# Revit family: Pojemnik_na_papier_toaletowy_ZEN S
name_source: partatom
category: Furniture
units: mm (PartAtom-declared; Revit-internal decimal feet)

## family parameters
Always vertical = Yes
Cut with Voids When Loaded = No
Host = Wall
Room Calculation Point = No
Shared = No

## types (1)
- Type 1
    Color / Kolor = White / Biały
    Depth / Glebokosc = 130 mm  [stored 0.426509 ft]
    Description = Pojemnik na papier toaletowy ZEN S wykonany jest z odpornego na uszkodzenia, białego plastiku ABS. Zaokrąglone brzegi gwarantują wygodę w jego czyszczeniu i konserwacji. Jest on przeznaczony do roli papieru o średnicy 18 - 23 cm; model ten poleca się do miejsc użytku publicznego o średnim i wysokim natężeniu ruchu. Poziom zużycia wkładu można łatwo kontrolować dzięki przeźroczystemu wizjerowi występującemu na przodzie obudowy. Dozownik do papieru toaletowego ZEN S to wysoce funkcjonalny i uniwersalny podajnik papieru toaletowego Jumbo, który z łatwością dopasowuje się do różnorodnych wnętrz.
    Height / Wysokosc = 290 mm  [stored 0.951444 ft]
    Manufacturer = FANECO.com
    Manufacturer code / Kod producenta = 5901764293620
    Material = plastic ABS, biały
    Material finish / Wykonczenie = Plastic ABS
    Model = ZEN S
    Product code / Kod produktu = LCP0204B
    Type Comments = Pojemnik na papier toaletowy ZEN S
    URL = https://faneco.com
    Weight / Waga = 0.77 kg
    Width / Szerokosc = 268 mm

note: [stored X ft] marks values corroborated as IEEE doubles in the binary element streams (Revit-internal decimal feet)

## geometry (parser evidence)
native form markers: Sweep x7
no freeform markers — native parametric forms only
